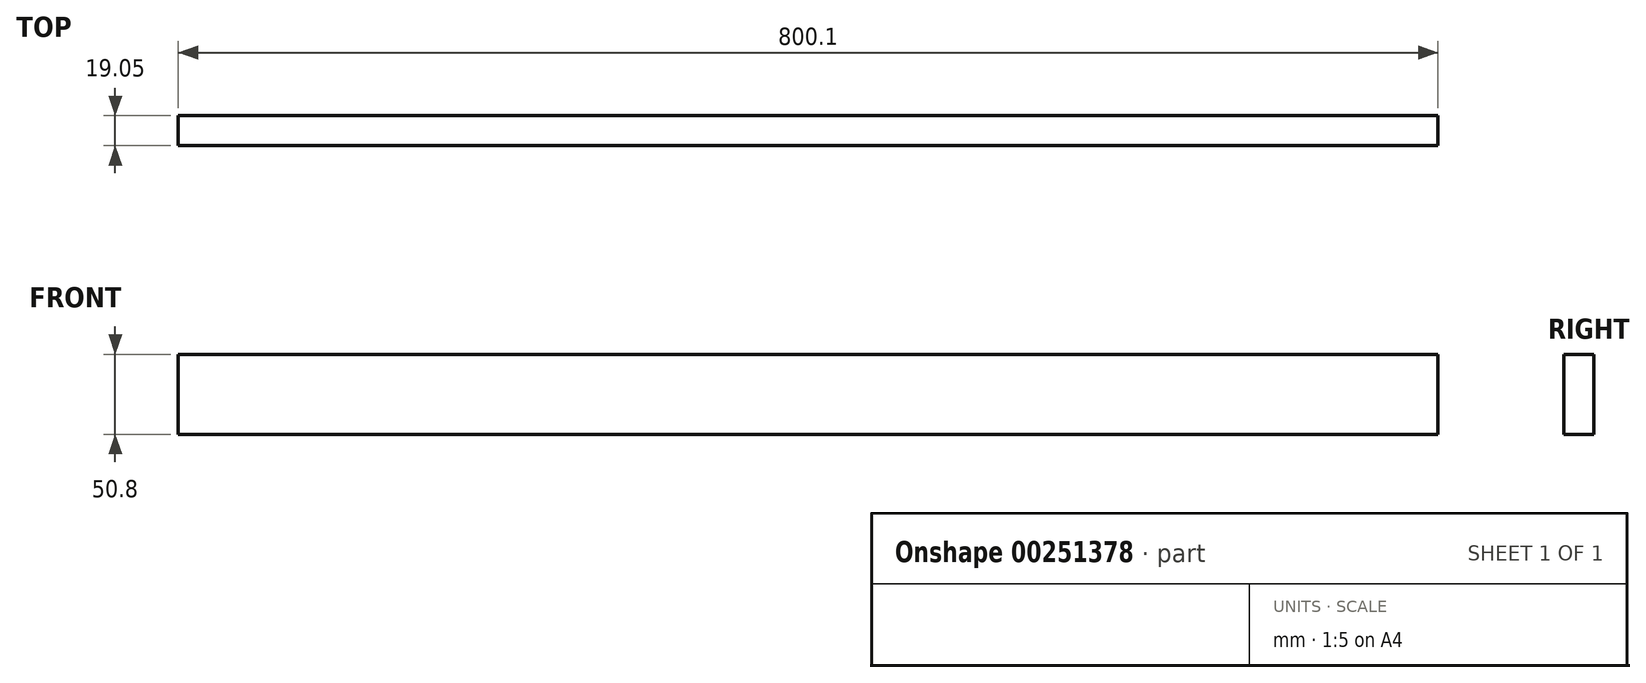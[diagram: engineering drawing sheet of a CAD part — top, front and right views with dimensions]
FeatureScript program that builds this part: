
annotation { "Feature Type Name" : "Feature", "Feature Type Description" : "" }
export const myFeature = defineFeature(function(context is Context, id is Id, definition is map)
    precondition{}
    {
        {
            var Q0;
            Q0=qCreatedBy(makeId("Front.planeOp"),FACE);
            var sketch = newSketch(context, id + "F0", { "sketchPlane" : qUnion([Q0])});
            skLineSegment(sketch, "E0.bottom", {"start": v(-400.05, 25.4) * mm, "end": v(400.05, 25.4) * mm});
            skLineSegment(sketch, "E0.top", {"start": v(-400.05, -25.4) * mm, "end": v(400.05, -25.4) * mm});
            skLineSegment(sketch, "E0.left", {"start": v(-400.05, 25.4) * mm, "end": v(-400.05, -25.4) * mm});
            skLineSegment(sketch, "E0.right", {"start": v(400.05, 25.4) * mm, "end": v(400.05, -25.4) * mm});
            skPoint(sketch, "E0.middle", {"position": v(0, 0) * mm});
            skSolve(sketch);
        }
        {
            var Q0;
            Q0 = qSketchRegion(id + "F0", true);
            extrude(context, id + "F1", {"entities" : qUnion([Q0]), "depth" : 19.05 * mm});
        }
    });
